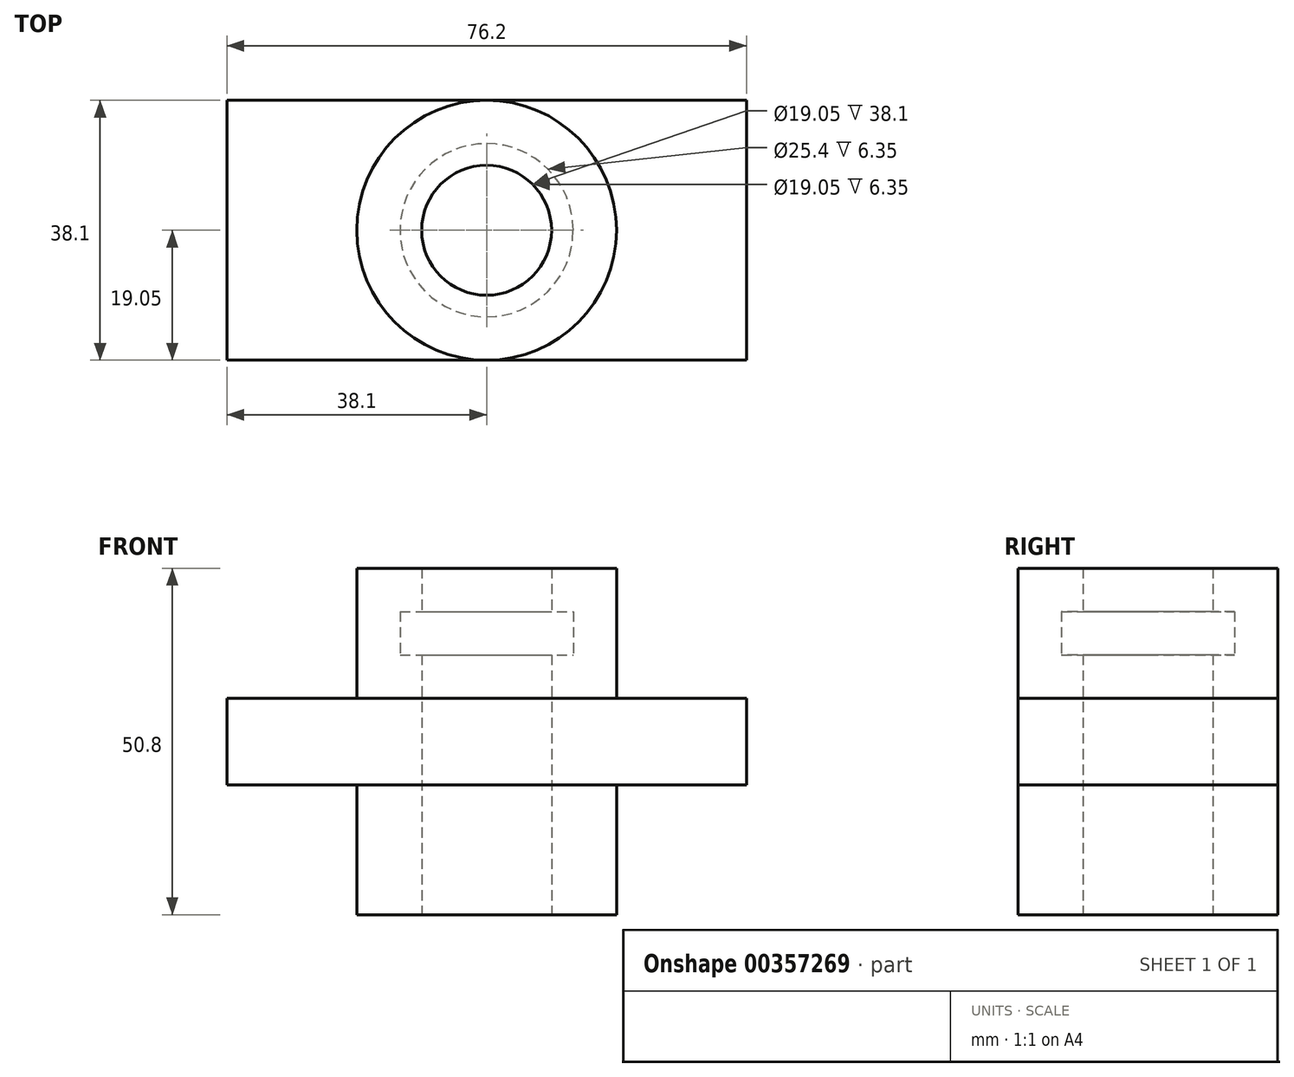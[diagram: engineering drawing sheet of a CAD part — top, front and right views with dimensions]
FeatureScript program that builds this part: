
annotation { "Feature Type Name" : "Feature", "Feature Type Description" : "" }
export const myFeature = defineFeature(function(context is Context, id is Id, definition is map)
    precondition{}
    {
        {
            var Q0;
            Q0=qCreatedBy(makeId("Front.planeOp"),FACE);
            var sketch = newSketch(context, id + "F0", { "sketchPlane" : qUnion([Q0])});
            skLineSegment(sketch, "E0.bottom", {"start": v(-38.1, 0) * mm, "end": v(38.1, 0) * mm});
            skLineSegment(sketch, "E0.top", {"start": v(-38.1, 12.7) * mm, "end": v(38.1, 12.7) * mm});
            skLineSegment(sketch, "E0.left", {"start": v(-38.1, 0) * mm, "end": v(-38.1, 12.7) * mm});
            skLineSegment(sketch, "E0.right", {"start": v(38.1, 0) * mm, "end": v(38.1, 12.7) * mm});
            skPoint(sketch, "E1", {"position": v(0, 0) * mm});
            skSolve(sketch);
        }
        {
            var Q0;
            Q0 = qSketchRegion(id + "F0", true);
            extrude(context, id + "F1", {"entities" : qUnion([Q0]), "endBound" : BoundingType.SYMMETRIC, "depth" : 38.1 * mm});
        }
        {
            var Q0;
            Q0=qCreatedBy(makeId("Top.planeOp"),FACE);
            var sketch = newSketch(context, id + "F2", { "sketchPlane" : qUnion([Q0])});
            skCircle(sketch, "E2", {"center": v(0, 0) * mm, "radius": 19.05 * mm});
            skSolve(sketch);
        }
        {
            var Q0;
            Q0=makeQuery(id+"F2.imprint","IMPRINT",FACE,{"disambiguationData":[TD([[makeQuery(id+"F2.imprint","IMPRINT",EDGE,{"derivedFrom":sQuery(id+"F2.wireOp",EDGE,"E2")}),1.0]])]});
            extrude(context, id + "F3", {"entities" : qUnion([Q0]), "operationType" : NewBodyOperationType.ADD, "oppositeDirection" : true, "depth" : 19.05 * mm});
        }
        {
            var Q0;
            Q0=makeQuery(id+"F1.opExtrude","SWEPT_FACE",FACE,{"disambiguationData":[OSD([sQuery(id+"F0.wireOp",EDGE,"E0.top")])]});
            var sketch = newSketch(context, id + "F4", { "sketchPlane" : qUnion([Q0])});
            skCircle(sketch, "E3", {"center": v(0, 0) * mm, "radius": 19.05 * mm});
            skSolve(sketch);
        }
        {
            var Q0;
            Q0 = qSketchRegion(id + "F4", true);
            extrude(context, id + "F5", {"entities" : qUnion([Q0]), "operationType" : NewBodyOperationType.ADD, "depth" : 19.05 * mm});
        }
        {
            var Q0;
            Q0=makeQuery(id+"F3.opExtrude","CAP_FACE",FACE,{"disambiguationData":[OSD([sQuery(id+"F2.wireOp",EDGE,"E2")])],"isStart":false});
            var sketch = newSketch(context, id + "F6", { "sketchPlane" : qUnion([Q0])});
            skCircle(sketch, "E4", {"center": v(0, 0) * mm, "radius": 9.53 * mm});
            skSolve(sketch);
        }
        {
            var Q0;
            Q0 = qSketchRegion(id + "F6", true);
            extrude(context, id + "F7", {"entities" : qUnion([Q0]), "operationType" : NewBodyOperationType.REMOVE, "oppositeDirection" : true, "depth" : 38.1 * mm});
        }
        {
            var Q0;
            Q0=makeQuery(id+"F7.boolean.opBoolean","COPY",FACE,{"derivedFrom":makeQuery(id+"F7.opExtrude","CAP_FACE",FACE,{"disambiguationData":[OSD([sQuery(id+"F6.wireOp",EDGE,"E4")])],"isStart":false})});
            var sketch = newSketch(context, id + "F8", { "sketchPlane" : qUnion([Q0])});
            skCircle(sketch, "E5", {"center": v(0, 0) * mm, "radius": 12.7 * mm});
            skSolve(sketch);
        }
        {
            var Q0;
            Q0 = qSketchRegion(id + "F8", true);
            extrude(context, id + "F9", {"entities" : qUnion([Q0]), "operationType" : NewBodyOperationType.REMOVE, "oppositeDirection" : true, "depth" : 6.35 * mm});
        }
        {
            var Q0;
            Q0=makeQuery(id+"F9.boolean.opBoolean","COPY",FACE,{"derivedFrom":makeQuery(id+"F9.opExtrude","CAP_FACE",FACE,{"disambiguationData":[OSD([sQuery(id+"F8.wireOp",EDGE,"E5")])],"isStart":false})});
            var sketch = newSketch(context, id + "F10", { "sketchPlane" : qUnion([Q0])});
            skCircle(sketch, "E6", {"center": v(0, 0) * mm, "radius": 9.53 * mm});
            skSolve(sketch);
        }
        {
            var Q0;
            Q0 = qSketchRegion(id + "F10", true);
            extrude(context, id + "F11", {"entities" : qUnion([Q0]), "operationType" : NewBodyOperationType.REMOVE, "oppositeDirection" : true, "depth" : 6.35 * mm});
        }
    });
